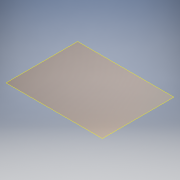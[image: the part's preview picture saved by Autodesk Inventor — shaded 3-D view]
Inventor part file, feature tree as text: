
AUTODESK INVENTOR PART (.ipt)
format: ipt  version: 2017 SP1 (Build 210196100, 196)  size: 83,968 bytes
history: native  units: mm
features: other x3, plane x1
ambient origin geometry x8: Origin, YZ Plane, XZ Plane, XY Plane, X Axis, Y Axis, Z Axis, Center Point
feature tree (4):
  plane  "Arbeitsebene1"
  other  "<userpath>\Dropbox\Elektronik\aXe_Dashboard240XL\Gehäuse\Montiert.iam"
  other  "Montiert.iam"
  other  "GehäuseDeckel:1"
